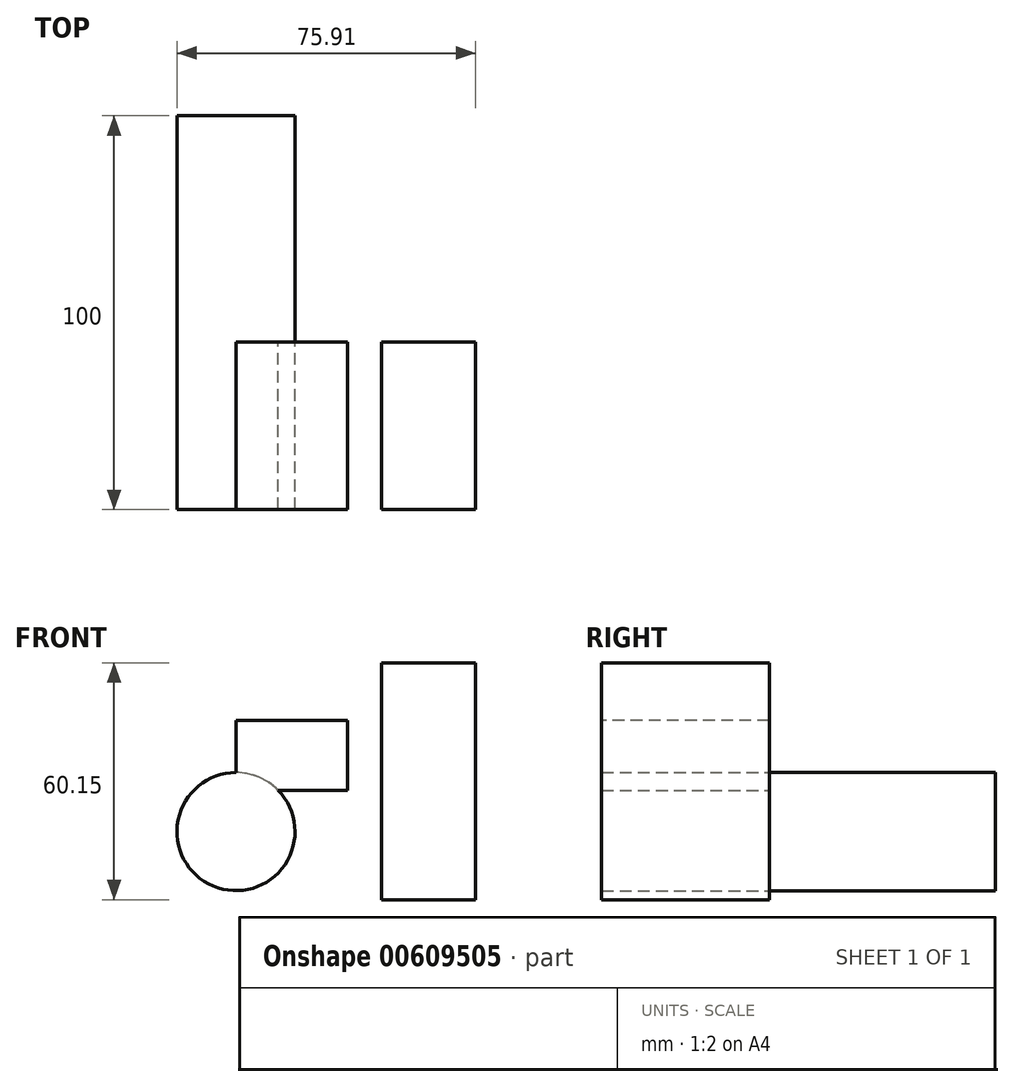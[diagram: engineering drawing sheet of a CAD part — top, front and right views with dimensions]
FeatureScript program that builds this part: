
annotation { "Feature Type Name" : "Feature", "Feature Type Description" : "" }
export const myFeature = defineFeature(function(context is Context, id is Id, definition is map)
    precondition{}
    {
        {
            var Q0;
            Q0=qCreatedBy(makeId("Front.planeOp"),FACE);
            var sketch = newSketch(context, id + "F0", { "sketchPlane" : qUnion([Q0])});
            skCircle(sketch, "E0", {"center": v(0, 0) * mm, "radius": 15 * mm});
            skSolve(sketch);
        }
        {
            var Q0;
            Q0 = qSketchRegion(id + "F0", true);
            extrude(context, id + "F1", {"entities" : qUnion([Q0]), "depth" : 100 * mm, "offsetDistance" : 25 * mm});
        }
        {
            var Q0;
            Q0=makeQuery(id+"F1.opExtrude","CAP_FACE",FACE,{"disambiguationData":[OSD([sQuery(id+"F0.wireOp",EDGE,"E0")])],"isStart":false});
            var sketch = newSketch(context, id + "F2", { "sketchPlane" : qUnion([Q0])});
            skSolve(sketch);
        }
        {
            var Q0;
            Q0=makeQuery(id+"F2.imprint","IMPRINT",FACE,{"disambiguationData":[TD([[makeQuery(id+"F2.imprint","IMPRINT",EDGE,{"derivedFrom":makeQuery(id+"F1.opExtrude","CAP_EDGE",EDGE,{"disambiguationData":[OSD([sQuery(id+"F0.wireOp",EDGE,"E0")])],"isStart":false})}),1.0]])]});
            var sketch = newSketch(context, id + "F3", { "sketchPlane" : qUnion([Q0])});
            skLineSegment(sketch, "E1.bottom", {"start": v(0, 10.53) * mm, "end": v(28.39, 10.53) * mm});
            skLineSegment(sketch, "E1.top", {"start": v(0, 28.2) * mm, "end": v(28.39, 28.2) * mm});
            skLineSegment(sketch, "E1.left", {"start": v(0, 10.53) * mm, "end": v(0, 28.2) * mm});
            skLineSegment(sketch, "E1.right", {"start": v(28.39, 10.53) * mm, "end": v(28.39, 28.2) * mm});
            skLineSegment(sketch, "E2.bottom", {"start": v(37.03, -17.3) * mm, "end": v(60.9, -17.3) * mm});
            skLineSegment(sketch, "E2.top", {"start": v(37.03, 42.86) * mm, "end": v(60.9, 42.86) * mm});
            skLineSegment(sketch, "E2.left", {"start": v(37.03, -17.3) * mm, "end": v(37.03, 42.86) * mm});
            skLineSegment(sketch, "E2.right", {"start": v(60.9, -17.3) * mm, "end": v(60.9, 42.86) * mm});
            skSolve(sketch);
        }
        {
            var Q0;
            Q0 = qSketchRegion(id + "F3", true);
            extrude(context, id + "F4", {"entities" : qUnion([Q0]), "operationType" : NewBodyOperationType.ADD, "oppositeDirection" : true, "depth" : 42.57 * mm, "offsetDistance" : 25 * mm});
        }
    });
